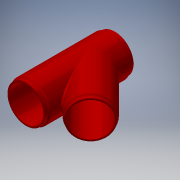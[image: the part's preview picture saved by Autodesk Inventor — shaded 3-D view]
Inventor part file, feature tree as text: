
AUTODESK INVENTOR PART (.ipt)
format: ipt  version: 2017.3 (Build 213257000, 257)  size: 292,864 bytes
history: native  units: in
note: dims shown in document units (in); Inventor stores cm internally (conversion verified against a paired STEP export)
features: extrude x18, sketch x14, fillet x6, chamfer x3, plane x1
ambient origin geometry x8: Origin, YZ Plane, XZ Plane, XY Plane, X Axis, Y Axis, Z Axis, Center Point
bodies: Solid1 (feature_tree)
feature tree (42):
  sketch  "Sketch1"  dims[d0=28.5in d1=31.0in]
  extrude  "Extrusion1"  Depth=31.0in
  plane  "Work Plane1"
  sketch  "Sketch2"  dims[d2=33.0in d3=52.9606in d4=19.4961in d5=0.0in d6=0.0in]
  extrude  "Extrusion2"  Depth=52.9606in TaperAngle=0.0deg
  extrude  "Extrusion3"  Depth=28.5in
  extrude  "Extrusion4"  Depth=33.0in
  extrude  "Extrusion5"  Depth=30.0in
  extrude  "Extrusion6"  Depth=30.0in
  extrude  "Extrusion7"  TaperAngle=0.0deg  [1 undecoded]
  extrude  "Extrusion8"  Depth=0.5in
  extrude  "Extrusion9"  Depth=49.9606in
  fillet  "Fillet1"  Radius=16.4961in
  fillet  "Fillet2"  [1 undecoded]
  fillet  "Fillet3"  Radius=49.9606in
  fillet  "Fillet4"  [1 undecoded]
  extrude  "Extrusion10"  TaperAngle=0.0deg  [1 undecoded]
  extrude  "Extrusion11"  TaperAngle=0.0deg  [1 undecoded]
  extrude  "Extrusion12"  Depth=6.0in
  fillet  "Fillet5"  Radius=1.0in
  chamfer  "Chamfer2"  Distance=1.0in
  fillet  "Fillet6"  Radius=32.48in
  chamfer  "Chamfer3"  Distance=1.0in
  extrude  "Extrusion13"  Depth=32.48in
  extrude  "Extrusion14"  Depth=1.0in TaperAngle=0.0deg
  extrude  "Extrusion15"  Depth=0.0312in
  chamfer  "Chamfer4"  Distance=0.74in
  extrude  "Extrusion16"  Depth=0.125in TaperAngle=45.0deg
  extrude  "Extrusion17"  Depth=0.0312in
  extrude  "Extrusion18"  Depth=0.0312in TaperAngle=45.0deg
  sketch  "Sketch3"  dims[d7=45.0deg d8=28.5in]
  sketch  "Sketch4"  dims[d9=31.0in d10=33.0in]
  sketch  "Sketch5"  dims[d11=52.9606in d12=0.0in d13=30.0in]
  sketch  "Sketch6"  dims[d14=0.5in d15=0.0in d16=30.0in]
  sketch  "Sketch7"  dims[d17=0.5in d18=0.0in]
  sketch  "Sketch8"  dims[d19=30.0in d20=0.5in]
  sketch  "Sketch9"  dims[d21=0.0in d22=49.9606in d23=16.4961in d24=0.0in d25=0.0in d26=49.9606in d27=0.0in]
  sketch  "Sketch10"  dims[d28=52.9606in d29=0.0in]
  sketch  "Sketch11"  dims[d30=52.9606in d31=0.0in]
  sketch  "Sketch12"  dims[d32=1.0in d33=6.0in d34=1.0in]
  sketch  "Sketch13"  dims[d35=1.0in]
  sketch  "Sketch14"  dims[d39=32.48in d40=1.0in d41=0.0in d42=32.48in d43=1.0in d44=0.0in d45=32.48in d46=1.0in d47=0.0in d48=0.0312in d49=0.74in d50=0.125in d51=45.0deg d52=0.0312in d53=0.0312in d54=0.125in d55=45.0deg d56=1.0in d57=0.0in d58=1.0in d59=0.0in d60=1.0in d61=0.0in d62=0.26in d64=0.125in d65=45.0deg d66=1.0in d67=0.0in d68=1.0in d69=0.0in d70=1.0in d71=0.0in]
note: 5 required parameter values undecoded (feature->parameter linkage not recoverable at this tier; creation-order binding heuristic only, values carry confidence <= 0.55)
